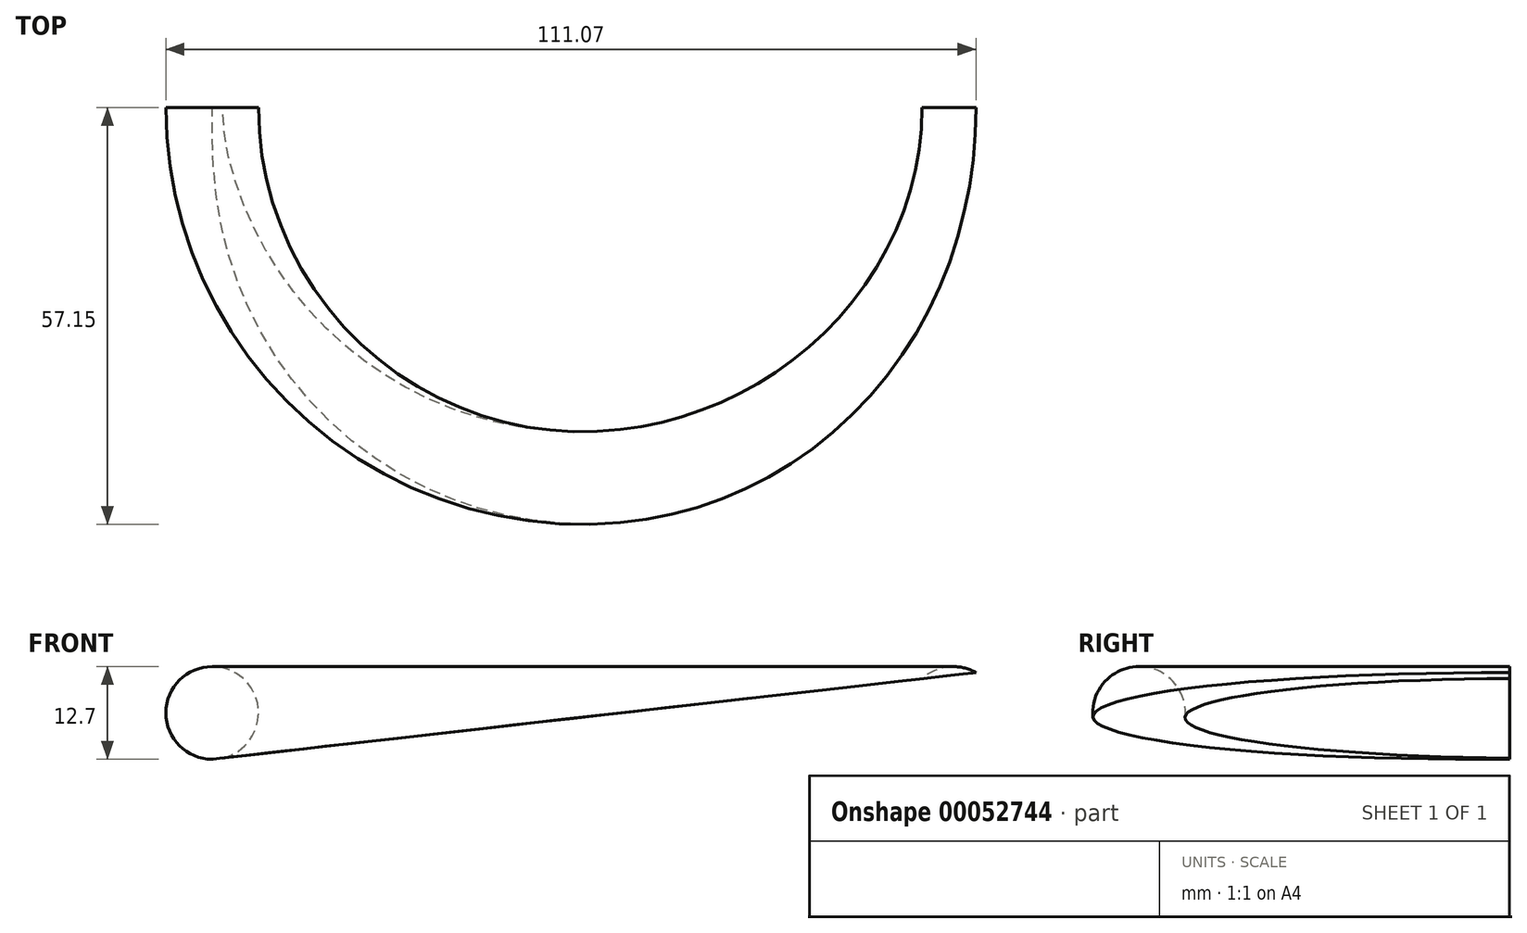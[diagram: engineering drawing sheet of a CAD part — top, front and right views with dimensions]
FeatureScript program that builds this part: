
annotation { "Feature Type Name" : "Feature", "Feature Type Description" : "" }
export const myFeature = defineFeature(function(context is Context, id is Id, definition is map)
    precondition{}
    {
        {
            var Q0;
            Q0=qCreatedBy(makeId("Front.planeOp"),FACE);
            var sketch = newSketch(context, id + "F0", { "sketchPlane" : qUnion([Q0])});
            skCircle(sketch, "E0", {"center": v(50.8, 0) * mm, "radius": 6.35 * mm});
            skLineSegment(sketch, "E1", {"start": v(0, 0) * mm, "end": v(50.8, 0) * mm, "construction": true});
            skSolve(sketch);
        }
        {
            var Q0;
            Q0=qCreatedBy(makeId("Right.planeOp"),FACE);
            var sketch = newSketch(context, id + "F1", { "sketchPlane" : qUnion([Q0])});
            skLineSegment(sketch, "E2", {"start": v(0, 0) * mm, "end": v(0, -72.37) * mm, "construction": true});
            skSolve(sketch);
        }
        {
            var Q0;
            Q0=qSketchRegion(id+"F0",true);
            var Q1;
            Q1=sQuery(id+"F1.wireOp",EDGE,"E2");
            revolve(context, id + "F2", {"entities" : qUnion([Q0]), "axis" : qUnion([Q1]), "revolveType" : RevolveType.ONE_DIRECTION, "angle" : 180 * degree});
        }
        {
            var Q0;
            Q0=qCreatedBy(makeId("Front.planeOp"),FACE);
            var sketch = newSketch(context, id + "F3", { "sketchPlane" : qUnion([Q0])});
            skLineSegment(sketch, "E3", {"start": v(-50.8, -6.35) * mm, "end": v(67.75, 7.1) * mm});
            skLineSegment(sketch, "E4", {"start": v(67.75, 7.1) * mm, "end": v(67.75, -6.35) * mm});
            skLineSegment(sketch, "E5", {"start": v(67.75, -6.35) * mm, "end": v(-50.8, -6.35) * mm});
            skSolve(sketch);
        }
        {
            var Q0;
            Q0 = qSketchRegion(id + "F3", true);
            extrude(context, id + "F4", {"entities" : qUnion([Q0]), "operationType" : NewBodyOperationType.REMOVE, "depth" : 63.5 * mm});
        }
    });
